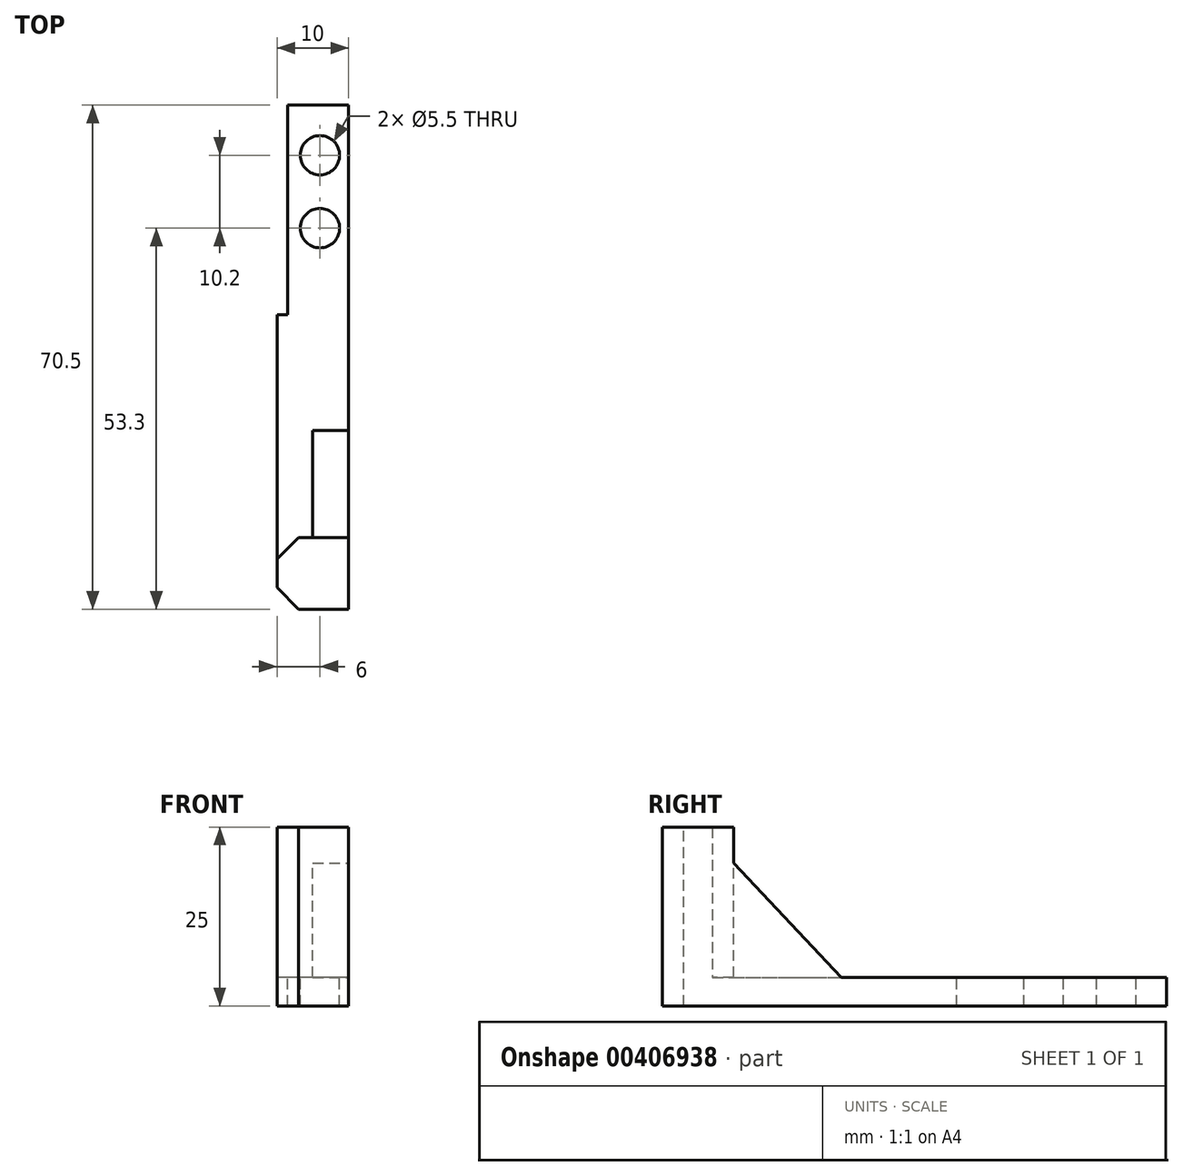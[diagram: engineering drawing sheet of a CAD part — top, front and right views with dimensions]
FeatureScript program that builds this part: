
annotation { "Feature Type Name" : "Feature", "Feature Type Description" : "" }
export const myFeature = defineFeature(function(context is Context, id is Id, definition is map)
    precondition{}
    {
        {
            var Q0;
            Q0=qCreatedBy(makeId("Right.planeOp"),FACE);
            var sketch = newSketch(context, id + "F0", { "sketchPlane" : qUnion([Q0])});
            skLineSegment(sketch, "E0.bottom", {"start": v(0, 0) * mm, "end": v(10, 0) * mm});
            skLineSegment(sketch, "E0.top", {"start": v(0, 25) * mm, "end": v(10, 25) * mm});
            skLineSegment(sketch, "E0.left", {"start": v(0, 0) * mm, "end": v(0, 25) * mm});
            skLineSegment(sketch, "E0.right", {"start": v(10, 0) * mm, "end": v(10, 25) * mm});
            skLineSegment(sketch, "E1.bottom", {"start": v(10, 0) * mm, "end": v(70.5, 0) * mm});
            skLineSegment(sketch, "E1.top", {"start": v(10, 4) * mm, "end": v(70.5, 4) * mm});
            skLineSegment(sketch, "E1.left", {"start": v(10, 0) * mm, "end": v(10, 4) * mm});
            skLineSegment(sketch, "E1.right", {"start": v(70.5, 0) * mm, "end": v(70.5, 4) * mm});
            skSolve(sketch);
        }
        {
            var Q0;
            Q0 = qSketchRegion(id + "F0", true);
            extrude(context, id + "F1", {"entities" : qUnion([Q0]), "depth" : 10 * mm});
        }
        {
            var Q0;
            Q0=makeQuery(id+"F1.opExtrude","SWEPT_FACE",FACE,{"disambiguationData":[OSD([sQuery(id+"F0.wireOp",EDGE,"E1.top")])]});
            var sketch = newSketch(context, id + "F2", { "sketchPlane" : qUnion([Q0])});
            skCircle(sketch, "E2", {"center": v(6, 63.5) * mm, "radius": 2.75 * mm});
            skCircle(sketch, "E3", {"center": v(6, 53.3) * mm, "radius": 2.75 * mm});
            skSolve(sketch);
        }
        {
            var Q0;
            Q0=makeQuery(id+"F2.imprint","IMPRINT",FACE,{"disambiguationData":[TD([[makeQuery(id+"F2.imprint","IMPRINT",EDGE,{"derivedFrom":sQuery(id+"F2.wireOp",EDGE,"E3")}),1.0]])]});
            var Q1;
            Q1=makeQuery(id+"F2.imprint","IMPRINT",FACE,{"disambiguationData":[TD([[makeQuery(id+"F2.imprint","IMPRINT",EDGE,{"derivedFrom":sQuery(id+"F2.wireOp",EDGE,"E2")}),1.0]])]});
            extrude(context, id + "F3", {"entities" : qUnion([Q0, Q1]), "operationType" : NewBodyOperationType.REMOVE, "oppositeDirection" : true, "depth" : 31.7 * mm});
        }
        {
            var Q0;
            Q0=makeQuery(id+"F1.opExtrude","CAP_EDGE",EDGE,{"disambiguationData":[OSD([sQuery(id+"F0.wireOp",EDGE,"E0.left")])],"isStart":true});
            var Q1;
            Q1=makeQuery(id+"F1.opExtrude","CAP_EDGE",EDGE,{"disambiguationData":[OSD([sQuery(id+"F0.wireOp",EDGE,"E0.right")])],"isStart":true});
            chamfer(context, id + "F4", {"entities" : qUnion([Q0, Q1]), "width" : 3 * mm, "tangentPropagation" : true});
        }
        {
            var Q0;
            Q0=makeQuery(id+"F1.opExtrude","CAP_FACE",FACE,{"disambiguationData":[OSD([sQuery(id+"F0.wireOp",EDGE,"E0.bottom"),sQuery(id+"F0.wireOp",EDGE,"E0.top"),sQuery(id+"F0.wireOp",EDGE,"E0.left"),sQuery(id+"F0.wireOp",EDGE,"E0.right"),sQuery(id+"F0.wireOp",EDGE,"E1.bottom"),sQuery(id+"F0.wireOp",EDGE,"E1.top"),sQuery(id+"F0.wireOp",EDGE,"E1.right")])],"isStart":true});
            var sketch = newSketch(context, id + "F5", { "sketchPlane" : qUnion([Q0])});
            skLineSegment(sketch, "E4.bottom", {"start": v(-70.5, 0) * mm, "end": v(-41.17, 0) * mm});
            skLineSegment(sketch, "E4.top", {"start": v(-70.5, 4) * mm, "end": v(-41.17, 4) * mm});
            skLineSegment(sketch, "E4.left", {"start": v(-70.5, 0) * mm, "end": v(-70.5, 4) * mm});
            skLineSegment(sketch, "E4.right", {"start": v(-41.17, 0) * mm, "end": v(-41.17, 4) * mm});
            skSolve(sketch);
        }
        {
            var Q0;
            Q0=makeQuery(id+"F5.imprint","IMPRINT",FACE,{"disambiguationData":[TD([[makeQuery(id+"F5.imprint","IMPRINT",EDGE,{"derivedFrom":sQuery(id+"F5.wireOp",EDGE,"E4.bottom")}),-1.0]])]});
            extrude(context, id + "F6", {"entities" : qUnion([Q0]), "operationType" : NewBodyOperationType.REMOVE, "oppositeDirection" : true, "depth" : 1.5 * mm});
        }
        {
            var Q0;
            Q0=makeQuery(id+"F1.opExtrude","CAP_FACE",FACE,{"disambiguationData":[OSD([sQuery(id+"F0.wireOp",EDGE,"E0.bottom"),sQuery(id+"F0.wireOp",EDGE,"E0.top"),sQuery(id+"F0.wireOp",EDGE,"E0.left"),sQuery(id+"F0.wireOp",EDGE,"E0.right"),sQuery(id+"F0.wireOp",EDGE,"E1.bottom"),sQuery(id+"F0.wireOp",EDGE,"E1.top"),sQuery(id+"F0.wireOp",EDGE,"E1.right")])],"isStart":false});
            var sketch = newSketch(context, id + "F7", { "sketchPlane" : qUnion([Q0])});
            skLineSegment(sketch, "E5", {"start": v(10, 20) * mm, "end": v(25, 4) * mm});
            skSolve(sketch);
        }
        {
            var Q0;
            {var subQ0=sQuery(id+"F7.wireOp",EDGE,"E5");Q0=makeQuery(id+"F7.imprint","IMPRINT",FACE,{"disambiguationData":[TD([[makeQuery(id+"F7.imprint","IMPRINT",EDGE,{"derivedFrom":subQ0}),-1.0]])]});}
            extrude(context, id + "F8", {"entities" : qUnion([Q0]), "operationType" : NewBodyOperationType.ADD, "oppositeDirection" : true, "depth" : 5 * mm});
        }
    });
